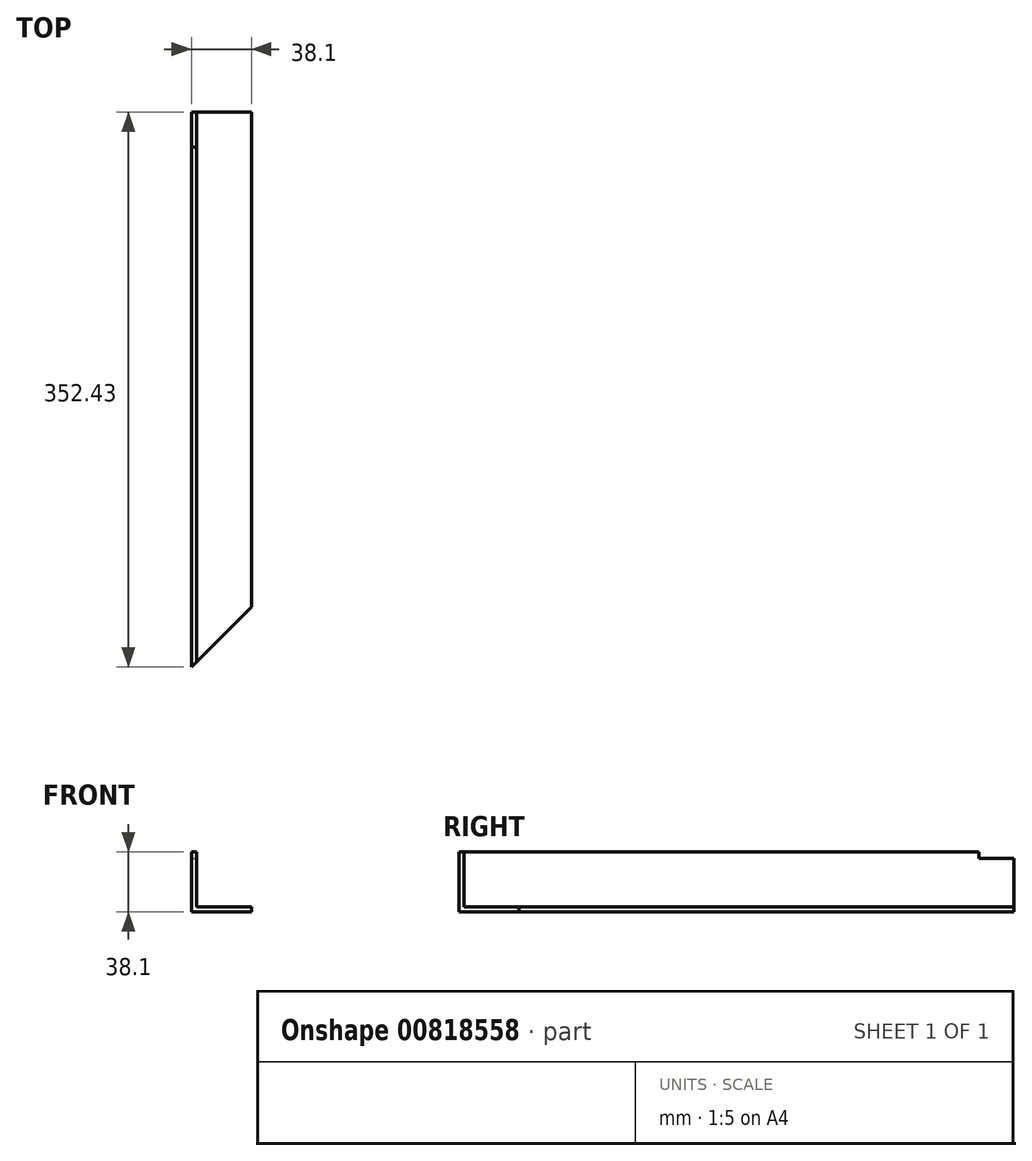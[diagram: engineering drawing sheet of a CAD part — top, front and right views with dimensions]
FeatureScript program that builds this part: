
annotation { "Feature Type Name" : "Feature", "Feature Type Description" : "" }
export const myFeature = defineFeature(function(context is Context, id is Id, definition is map)
    precondition{}
    {
        {
            var Q0;
            Q0=qCreatedBy(makeId("Front.planeOp"),FACE);
            var sketch = newSketch(context, id + "F0", { "sketchPlane" : qUnion([Q0])});
            skLineSegment(sketch, "E0", {"start": v(-21.73, 20.45) * mm, "end": v(-21.73, -17.65) * mm});
            skLineSegment(sketch, "E1", {"start": v(-21.73, -17.65) * mm, "end": v(16.37, -17.65) * mm});
            skLineSegment(sketch, "E2", {"start": v(16.37, -17.65) * mm, "end": v(16.37, -14.47) * mm});
            skLineSegment(sketch, "E3", {"start": v(16.37, -14.47) * mm, "end": v(-18.55, -14.47) * mm});
            skLineSegment(sketch, "E4", {"start": v(-18.55, -14.47) * mm, "end": v(-18.55, 20.45) * mm});
            skLineSegment(sketch, "E5", {"start": v(-18.55, 20.45) * mm, "end": v(-21.73, 20.45) * mm});
            skSolve(sketch);
        }
        {
            var Q0;
            Q0=makeQuery(id+"F0.imprint","IMPRINT",FACE,{"disambiguationData":[TD([[makeQuery(id+"F0.imprint","IMPRINT",EDGE,{"derivedFrom":sQuery(id+"F0.wireOp",EDGE,"E0")}),1.0]])]});
            extrude(context, id + "F1", {"entities" : qUnion([Q0]), "depth" : 352.42 * mm, "offsetDistance" : 25.4 * mm});
        }
        {
            var Q0;
            Q0=makeQuery(id+"F1.opExtrude","SWEPT_FACE",FACE,{"disambiguationData":[OSD([sQuery(id+"F0.wireOp",EDGE,"E4")])]});
            var sketch = newSketch(context, id + "F2", { "sketchPlane" : qUnion([Q0])});
            skLineSegment(sketch, "E6", {"start": v(0, 16.48) * mm, "end": v(-22.23, 16.48) * mm});
            skLineSegment(sketch, "E7", {"start": v(-22.23, 16.48) * mm, "end": v(-22.23, 20.45) * mm});
            skLineSegment(sketch, "E8", {"start": v(-22.23, 20.45) * mm, "end": v(0, 20.45) * mm});
            skLineSegment(sketch, "E9", {"start": v(0, 20.45) * mm, "end": v(0, 16.48) * mm});
            skSolve(sketch);
        }
        {
            var Q0;
            Q0 = qSketchRegion(id + "F2", true);
            extrude(context, id + "F3", {"entities" : qUnion([Q0]), "operationType" : NewBodyOperationType.REMOVE, "oppositeDirection" : true, "depth" : 25.4 * mm, "offsetDistance" : 25.4 * mm});
        }
        {
            var Q0;
            Q0=makeQuery(id+"F1.opExtrude","SWEPT_FACE",FACE,{"disambiguationData":[OSD([sQuery(id+"F0.wireOp",EDGE,"E1")])]});
            var sketch = newSketch(context, id + "F4", { "sketchPlane" : qUnion([Q0])});
            skLineSegment(sketch, "E10", {"start": v(-21.73, 352.43) * mm, "end": v(16.37, 352.43) * mm});
            skLineSegment(sketch, "E11", {"start": v(16.37, 352.43) * mm, "end": v(16.37, 314.33) * mm});
            skLineSegment(sketch, "E12", {"start": v(16.37, 314.33) * mm, "end": v(-21.73, 352.43) * mm});
            skSolve(sketch);
        }
        {
            var Q0;
            Q0 = qSketchRegion(id + "F4", true);
            extrude(context, id + "F5", {"entities" : qUnion([Q0]), "operationType" : NewBodyOperationType.REMOVE, "oppositeDirection" : true, "depth" : 38.1 * mm, "offsetDistance" : 25.4 * mm});
        }
    });
